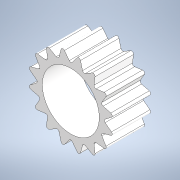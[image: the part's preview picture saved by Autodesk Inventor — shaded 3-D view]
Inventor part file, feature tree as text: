
AUTODESK INVENTOR PART (.ipt)
format: ipt  version: 2022.3 (Build 263350000, 350)  size: 424,960 bytes
history: native  units: mm
features: projected_geometry x4, extrude x2, sketch x2, imported_body x1
ambient origin geometry x8: Origin, YZ Plane, XZ Plane, XY Plane, X Axis, Y Axis, Z Axis, Center Point
bodies: Solid1 (feature_tree)
feature tree (9):
  extrude  "Extrusion1"  Depth=10.0mm TaperAngle=0.0deg
  extrude  "Extrusion2"  [1 undecoded]
  sketch  "Sketch1"  dims[d0=10.0mm d1=0.0mm d2=10.0mm d3=0.0mm]
  projected_geometry  "Projected Loop1"
  projected_geometry  "Projected Loop2"
  projected_geometry  "Projected Loop3"
  sketch  "Sketch2"
  projected_geometry  "Projected Loop4"
  imported_body  "Base1"
note: 1 required parameter value undecoded (feature->parameter linkage not recoverable at this tier; creation-order binding heuristic only, values carry confidence <= 0.55)
